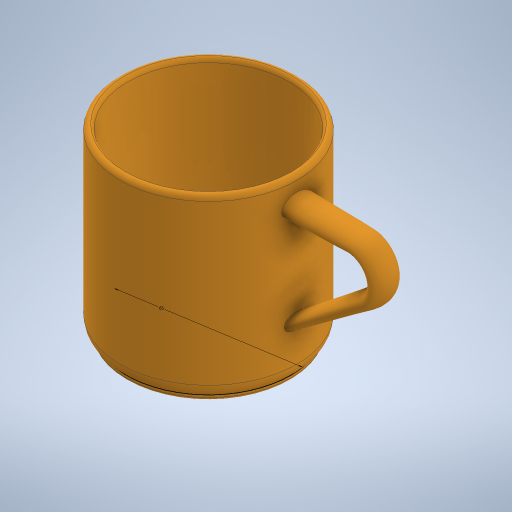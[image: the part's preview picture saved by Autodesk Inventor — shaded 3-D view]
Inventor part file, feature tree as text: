
AUTODESK INVENTOR PART (.ipt)
format: ipt  version: 2024 (Build 280153000, 153)  size: 389,632 bytes
history: native  units: mm
features: sketch x6, other x4, plane x2, fillet x2, extrude x2, revolve x1, shell x1, loft x1
ambient origin geometry x8: Origin, YZ Plane, XZ Plane, XY Plane, X Axis, Y Axis, Z Axis, Center Point
bodies: Body1 (feature_tree)
feature tree (19):
  other  "Sección transversal1"
  other  "Sólido1"
  revolve  "Revolución1"  [1 undecoded]
  shell  "Vaciado1"  Thickness=35.0mm
  sketch  "Boceto2"  dims[d3=65.0mm d4=90.0deg d5=3.0mm]
  other  "Punto de trabajo1"
  other  "Punto de trabajo2"
  plane  "Plano de trabajo1"
  sketch  "Boceto3"  dims[d6=0.5mm d7=2.0mm d8=0.0mm d9=20.0mm d10=25.0mm]
  plane  "Plano de trabajo2"
  loft  "Solevación1"
  fillet  "Empalme1"  Radius=3.0mm
  sketch  "Boceto5"  dims[d14=6.0mm]
  extrude  "Extrusión1"  Depth=2.0mm
  extrude  "Extrusión2"  Depth=10.0mm
  fillet  "Empalme2"  Radius=4.0mm
  sketch  "Boceto1"  dims[d0=32.5mm d1=70.0mm d2=35.0mm]
  sketch  "Boceto4"  dims[d11=10.0mm d12=15.0mm d13=4.0mm]
  sketch  "Boceto6"  dims[d15=3.0mm d16=5.0mm d17=0.0mm d18=90.0deg d19=0.0mm d20=90.0deg d21=0.0mm d22=90.0deg d23=2.0mm d24=65.0mm d26=2.0mm d27=0.0mm d28=62.0mm d29=2.0mm d30=0.0mm d31=1.0mm]
note: 1 required parameter value undecoded (feature->parameter linkage not recoverable at this tier; creation-order binding heuristic only, values carry confidence <= 0.55)
